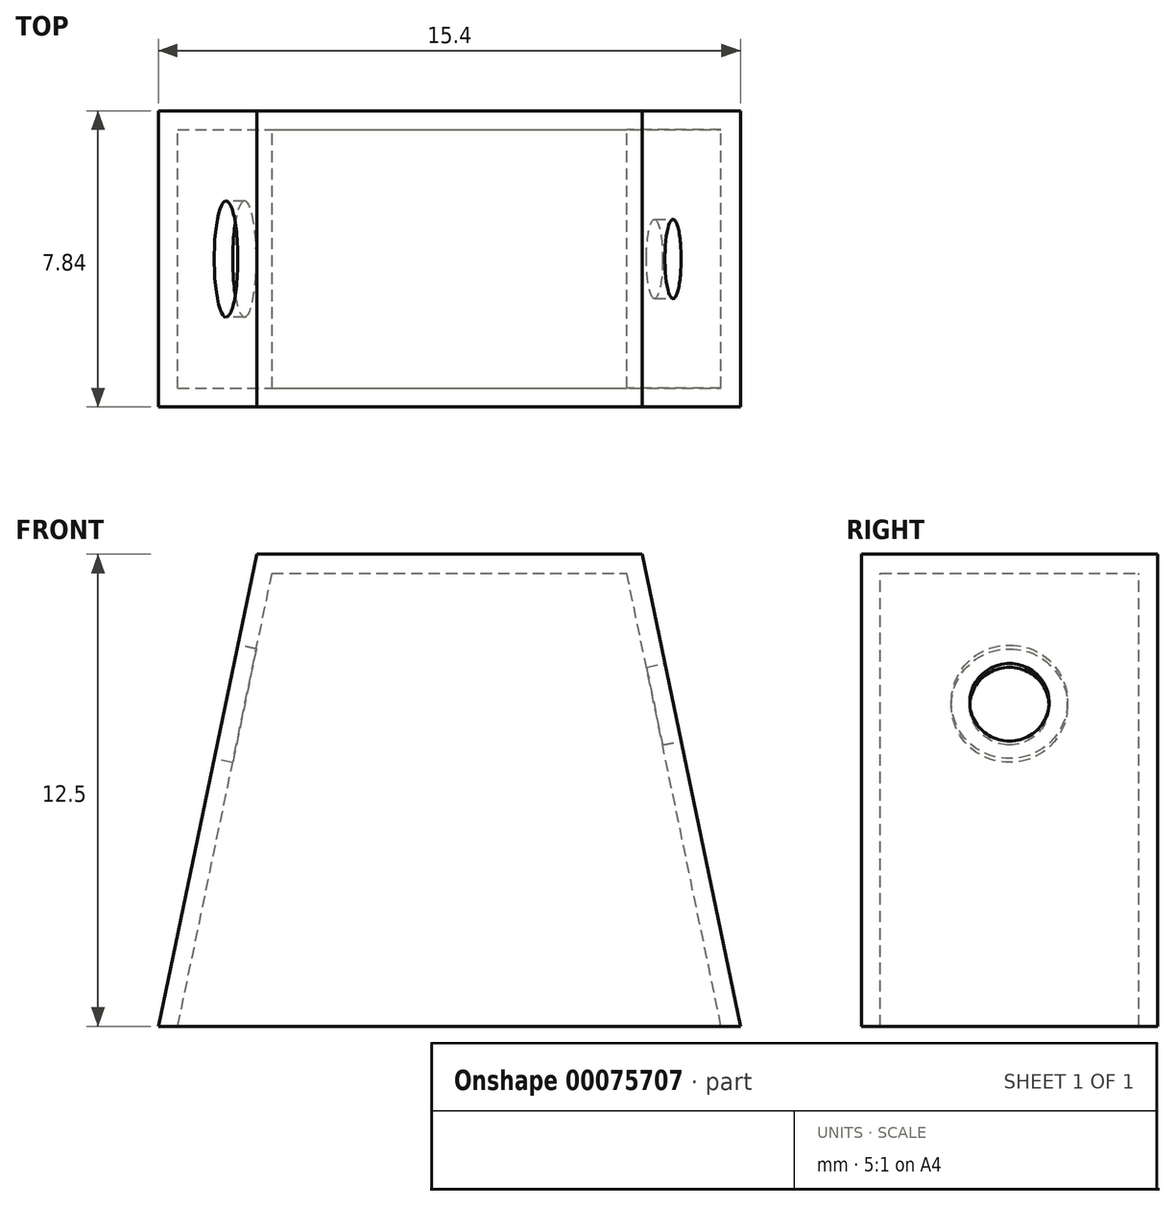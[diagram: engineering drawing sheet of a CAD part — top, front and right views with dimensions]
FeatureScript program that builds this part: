
annotation { "Feature Type Name" : "Feature", "Feature Type Description" : "" }
export const myFeature = defineFeature(function(context is Context, id is Id, definition is map)
    precondition{}
    {
        {
            var Q0;
            Q0=qCreatedBy(makeId("Front.planeOp"),FACE);
            var sketch = newSketch(context, id + "F0", { "sketchPlane" : qUnion([Q0])});
            skLineSegment(sketch, "E0", {"start": v(0, 0) * mm, "end": v(15.4, 0) * mm});
            skLineSegment(sketch, "E1", {"start": v(15.4, 0) * mm, "end": v(12.8, 12.5) * mm});
            skLineSegment(sketch, "E2", {"start": v(0, 0) * mm, "end": v(2.6, 12.5) * mm});
            skLineSegment(sketch, "E3", {"start": v(2.6, 12.5) * mm, "end": v(12.8, 12.5) * mm});
            skLineSegment(sketch, "E4", {"start": v(7.7, 0) * mm, "end": v(7.7, 12.5) * mm, "construction": true});
            skPoint(sketch, "E4.endSnap0", {"position": v(7.7, 12.5) * mm});
            skSolve(sketch);
        }
        {
            var Q0;
            Q0=makeQuery(id+"F0.imprint","IMPRINT",FACE,{"disambiguationData":[TD([[makeQuery(id+"F0.imprint","IMPRINT",EDGE,{"derivedFrom":sQuery(id+"F0.wireOp",EDGE,"E0")}),1.0]])]});
            extrude(context, id + "F1", {"entities" : qUnion([Q0]), "depth" : 7.84 * mm});
        }
        {
            var Q0;
            Q0=makeQuery(id+"F1.opExtrude","SWEPT_FACE",FACE,{"disambiguationData":[OSD([sQuery(id+"F0.wireOp",EDGE,"E1")])]});
            var sketch = newSketch(context, id + "F2", { "sketchPlane" : qUnion([Q0])});
            skCircle(sketch, "E5", {"center": v(-3.92, 5.63) * mm, "radius": 1.05 * mm});
            skPoint(sketch, "E5.centerSnap0", {"position": v(-3.92, 9.63) * mm});
            skSolve(sketch);
        }
        {
            var Q0;
            Q0=makeQuery(id+"F1.opExtrude","SWEPT_FACE",FACE,{"disambiguationData":[OSD([sQuery(id+"F0.wireOp",EDGE,"E0")])]});
            shell(context, id + "F3", {"entities" : qUnion([Q0]), "thickness" : .5 * mm});
        }
        {
            var Q0;
            Q0=makeQuery(id+"F2.imprint","IMPRINT",FACE,{"disambiguationData":[TD([[makeQuery(id+"F2.imprint","IMPRINT",EDGE,{"derivedFrom":sQuery(id+"F2.wireOp",EDGE,"E5")}),1.0]])]});
            extrude(context, id + "F4", {"entities" : qUnion([Q0]), "operationType" : NewBodyOperationType.REMOVE, "endBound" : BoundingType.UP_TO_NEXT, "oppositeDirection" : true, "depth" : 25 * mm});
        }
        {
            var Q0;
            Q0=makeQuery(id+"F1.opExtrude","SWEPT_FACE",FACE,{"disambiguationData":[OSD([sQuery(id+"F0.wireOp",EDGE,"E2")])]});
            var sketch = newSketch(context, id + "F5", { "sketchPlane" : qUnion([Q0])});
            skCircle(sketch, "E6", {"center": v(3.92, 8.78) * mm, "radius": 1.54 * mm});
            skPoint(sketch, "E6.centerSnap0", {"position": v(3.92, 12.77) * mm});
            skSolve(sketch);
        }
        {
            var Q0;
            Q0=makeQuery(id+"F5.imprint","IMPRINT",FACE,{"disambiguationData":[TD([[makeQuery(id+"F5.imprint","IMPRINT",EDGE,{"derivedFrom":sQuery(id+"F5.wireOp",EDGE,"E6")}),1.0]])]});
            var Q1;
            Q1=sQuery(id+"F5.wireOp",EDGE,"E6");
            extrude(context, id + "F6", {"entities" : qUnion([Q0]), "operationType" : NewBodyOperationType.REMOVE, "surfaceEntities" : qUnion([Q1]), "endBound" : BoundingType.UP_TO_NEXT, "oppositeDirection" : true, "depth" : 25 * mm});
        }
    });
